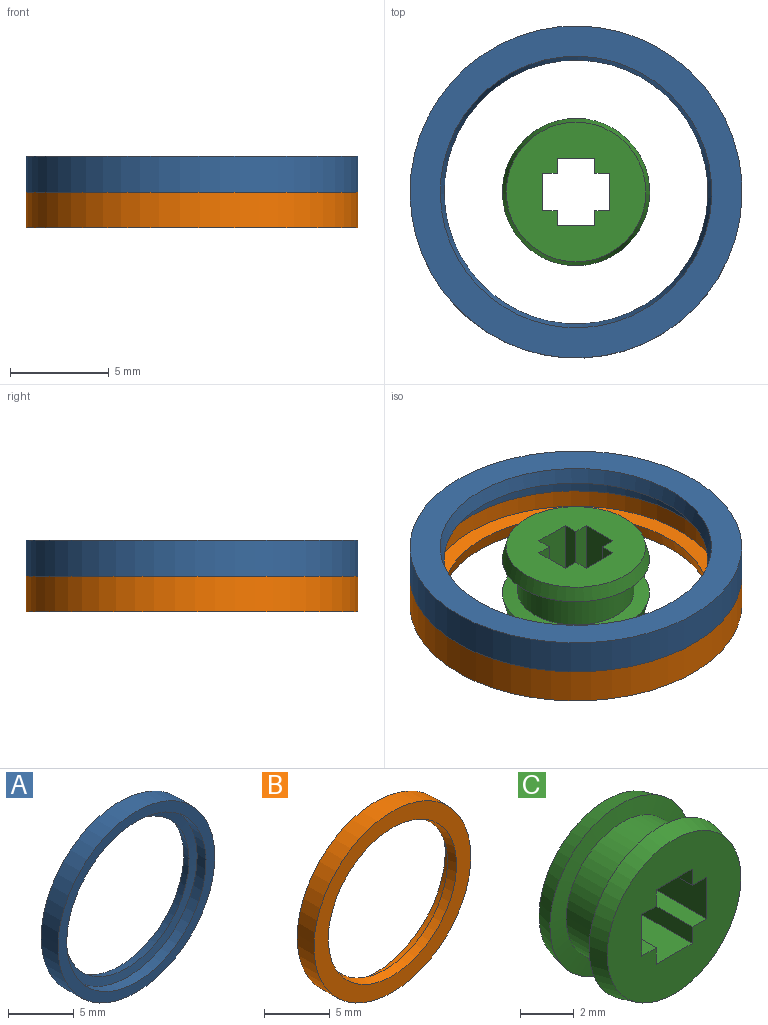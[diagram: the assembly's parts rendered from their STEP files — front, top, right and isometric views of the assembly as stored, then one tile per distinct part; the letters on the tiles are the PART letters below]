
ASSEMBLY  parts=3 mates=2
PART A: 6 faces, bbox 16.8x1.8x16.8 mm
  f0: plane 16.8x16.8mm, normal (0,-1,0), area 46.7mm2, adj f1,f5
  f1: cylinder r=8.4mm len=16.8mm, axis (0,-1,0), area 95mm2, adj f0,f2
  f2: plane 16.8x16.8mm, normal (0,1,0), area 73.4mm2, adj f1,f3
  f3: cone r=6.67mm half-angle=14.3deg, axis (0,1,0), area 33.7mm2, adj f2,f4
  f4: cone r=7.46mm half-angle=84.3deg, axis (0,-1,0), area 35.2mm2, adj f3,f5
  f5: cylinder r=7.46mm len=14.93mm, axis (0,-1,0), area 44.7mm2, adj f0,f4
PART B: 6 faces, bbox 16.8x1.8x16.8 mm
  f0: plane 16.8x16.8mm, normal (0,1,0), area 46.7mm2, adj f1,f5
  f1: cylinder r=8.4mm len=16.8mm, axis (0,1,0), area 95mm2, adj f0,f2
  f2: plane 16.8x16.8mm, normal (0,-1,0), area 73.4mm2, adj f1,f3
  f3: cone r=6.67mm half-angle=14.3deg, axis (0,-1,0), area 33.7mm2, adj f2,f4
  f4: cone r=7.46mm half-angle=84.3deg, axis (0,1,0), area 35.2mm2, adj f3,f5
  f5: cylinder r=7.46mm len=14.93mm, axis (0,1,0), area 44.7mm2, adj f0,f4
PART C: 19 faces, bbox 7.5x3.6x7.5 mm
  f0: cone r=3.53mm half-angle=14.3deg, axis (0,-1,0), area 18.1mm2, adj f1,f3
  f1: plane 7.06x7.06mm, normal (0,1,0), area 29.8mm2, adj f0,f7,f8,f9,f10,f11,f12,f13
  f2: cylinder r=2.94mm len=5.88mm, axis (0,-1,0), area 35.2mm2, adj f3,f6
  f3: cone r=3.73mm half-angle=84.3deg, axis (0,1,0), area 16.6mm2, adj f0,f2
  f4: cone r=3.53mm half-angle=14.3deg, axis (0,1,0), area 18.1mm2, adj f5,f6
  f5: plane 7.06x7.06mm, normal (0,-1,0), area 29.8mm2, adj f4,f7,f8,f9,f10,f11,f12,f13
  f6: cone r=3.73mm half-angle=84.3deg, axis (0,-1,0), area 16.6mm2, adj f2,f4
  f7: plane 3.6x0.75mm, normal (-1,0,0), area 2.7mm2, adj f1,f5,f8,f12
  f8: plane 3.6x0.75mm, normal (0,0,-1), area 2.7mm2, adj f1,f5,f7,f9
  f9: plane 3.6x1.9mm, normal (-1,0,0), area 6.8mm2, adj f1,f5,f8,f10
  f10: plane 3.6x0.75mm, normal (0,0,1), area 2.7mm2, adj f1,f5,f9,f11
  f11: plane 3.6x0.75mm, normal (-1,0,0), area 2.7mm2, adj f1,f5,f10,f13
  f12: plane 3.6x1.9mm, normal (0,0,-1), area 6.8mm2, adj f1,f5,f7,f14
  f13: plane 3.6x1.9mm, normal (0,0,1), area 6.8mm2, adj f1,f5,f11,f15
  f14: plane 3.6x0.75mm, normal (1,0,0), area 2.7mm2, adj f1,f5,f12,f17
  f15: plane 3.6x0.75mm, normal (1,0,0), area 2.7mm2, adj f1,f5,f13,f16
  f16: plane 3.6x0.75mm, normal (0,0,1), area 2.7mm2, adj f1,f5,f15,f18
  f17: plane 3.6x0.75mm, normal (0,0,-1), area 2.7mm2, adj f1,f5,f14,f18
  f18: plane 3.6x1.9mm, normal (1,0,0), area 6.8mm2, adj f1,f5,f16,f17
PLACE A rot(axis=(0.03,0.71,0.71),177deg) t=(0,0,-1.8)mm
PLACE B rot(axis=(0.03,0.71,0.71),177deg) t=(0,0,-1.8)mm
PLACE C rot(axis=(1,0,0),90deg) t=(0,0,-1.8)mm
MATE fastened B.f1 <-> A.f1  axis (0,0,1) through (0,0,-1.8)mm
MATE revolute C.f0 <-> B.f1  axis (0,0,-1) through (0,0,-3.6)mm
